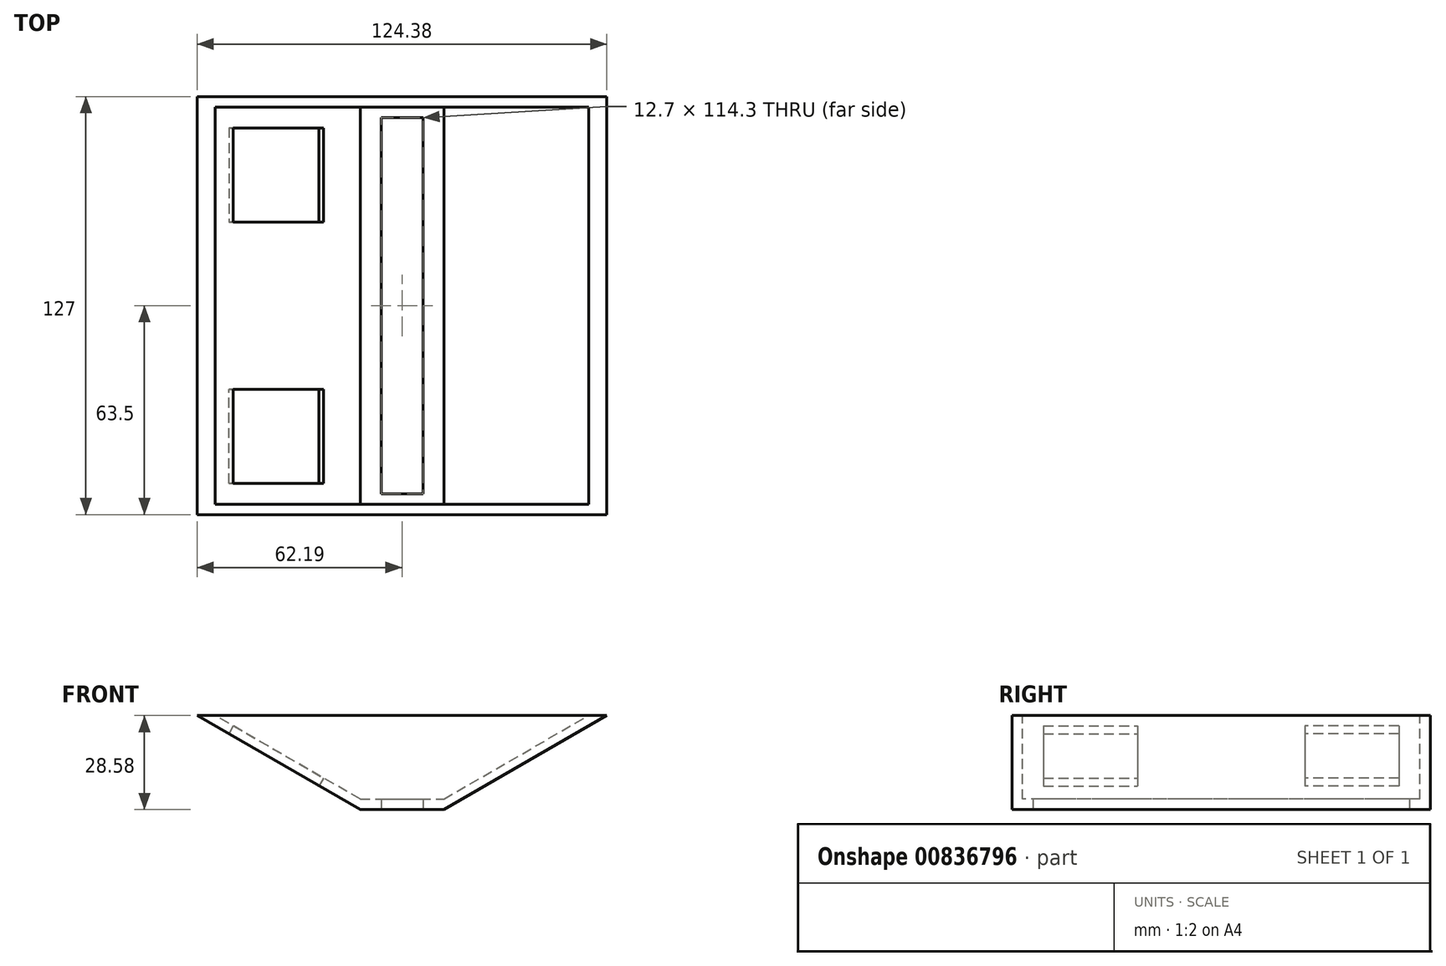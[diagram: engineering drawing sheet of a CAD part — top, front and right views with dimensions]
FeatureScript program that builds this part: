
annotation { "Feature Type Name" : "Feature", "Feature Type Description" : "" }
export const myFeature = defineFeature(function(context is Context, id is Id, definition is map)
    precondition{}
    {
        {
            var Q0;
            Q0=qCreatedBy(makeId("Top.planeOp"),FACE);
            var sketch = newSketch(context, id + "F0", { "sketchPlane" : qUnion([Q0])});
            skLineSegment(sketch, "E0.bottom", {"start": v(-12.7, 63.5) * mm, "end": v(12.7, 63.5) * mm});
            skLineSegment(sketch, "E0.top", {"start": v(-12.7, -63.5) * mm, "end": v(12.7, -63.5) * mm});
            skLineSegment(sketch, "E0.left", {"start": v(-12.7, 63.5) * mm, "end": v(-12.7, -63.5) * mm});
            skLineSegment(sketch, "E0.right", {"start": v(12.7, 63.5) * mm, "end": v(12.7, -63.5) * mm});
            skLineSegment(sketch, "E1.bottom", {"start": v(-6.35, 57.15) * mm, "end": v(6.35, 57.15) * mm});
            skLineSegment(sketch, "E1.top", {"start": v(-6.35, -57.15) * mm, "end": v(6.35, -57.15) * mm});
            skLineSegment(sketch, "E1.left", {"start": v(-6.35, 57.15) * mm, "end": v(-6.35, -57.15) * mm});
            skLineSegment(sketch, "E1.right", {"start": v(6.35, 57.15) * mm, "end": v(6.35, -57.15) * mm});
            skSolve(sketch);
        }
        {
            var Q0;
            Q0 = qSketchRegion(id + "F0", true);
            extrude(context, id + "F1", {"entities" : qUnion([Q0]), "depth" : 3.17 * mm, "offsetDistance" : 25.4 * mm});
        }
        {
            var Q0;
            Q0=qCreatedBy(makeId("Front.planeOp"),FACE);
            var sketch = newSketch(context, id + "F2", { "sketchPlane" : qUnion([Q0])});
            skLineSegment(sketch, "E2", {"start": v(12.7, 3.18) * mm, "end": v(56.7, 28.58) * mm});
            skLineSegment(sketch, "E3", {"start": v(12.7, 3.17) * mm, "end": v(56.7, 3.17) * mm});
            skLineSegment(sketch, "E4", {"start": v(12.7, 0) * mm, "end": v(62.2, 28.58) * mm});
            skLineSegment(sketch, "E5", {"start": v(56.7, 28.58) * mm, "end": v(62.2, 28.58) * mm});
            skLineSegment(sketch, "E6.MirrorCS", {"start": v(-56.7, 28.58) * mm, "end": v(-62.2, 28.58) * mm});
            skLineSegment(sketch, "E7.MirrorCS", {"start": v(-12.7, 0) * mm, "end": v(-62.2, 28.58) * mm});
            skLineSegment(sketch, "E8.MirrorCS", {"start": v(-12.7, 3.17) * mm, "end": v(-56.7, 28.58) * mm});
            skLineSegment(sketch, "E9", {"start": v(-12.7, 0) * mm, "end": v(-12.7, 3.18) * mm});
            skLineSegment(sketch, "E10", {"start": v(12.7, 3.18) * mm, "end": v(12.7, 0) * mm});
            skSolve(sketch);
        }
        {
            var Q0;
            Q0 = qSketchRegion(id + "F2", true);
            extrude(context, id + "F3", {"entities" : qUnion([Q0]), "operationType" : NewBodyOperationType.ADD, "depth" : 63.5 * mm, "offsetDistance" : 25.4 * mm, "hasSecondDirection" : true, "secondDirectionOppositeDirection" : true, "secondDirectionDepth" : 63.5 * mm});
        }
        {
            var Q0;
            Q0=qCreatedBy(makeId("Front.planeOp"),FACE);
            cPlane(context, id + "F4", {"entities" : qUnion([Q0]), "cplaneType" : CPlaneType.OFFSET, "offset" : 63.5 * mm, "width" : 152.4 * mm, "height" : 152.4 * mm});
        }
        {
            var Q0;
            Q0=qCreatedBy(makeId("Front.planeOp"),FACE);
            cPlane(context, id + "F5", {"entities" : qUnion([Q0]), "cplaneType" : CPlaneType.OFFSET, "offset" : 63.5 * mm, "oppositeDirection" : true, "width" : 152.4 * mm, "height" : 152.4 * mm});
        }
        {
            var Q0;
            Q0=qCreatedBy(id+"F4.planeOp",FACE);
            var sketch = newSketch(context, id + "F6", { "sketchPlane" : qUnion([Q0])});
            skLineSegment(sketch, "E11", {"start": v(-62.2, 28.58) * mm, "end": v(62.2, 28.58) * mm});
            skLineSegment(sketch, "E12", {"start": v(-62.2, 28.58) * mm, "end": v(-12.7, 0) * mm});
            skLineSegment(sketch, "E13", {"start": v(-12.7, 0) * mm, "end": v(12.7, 0) * mm});
            skLineSegment(sketch, "E14", {"start": v(12.7, 0) * mm, "end": v(62.2, 28.58) * mm});
            skSolve(sketch);
        }
        {
            var Q0;
            Q0 = qSketchRegion(id + "F6", true);
            extrude(context, id + "F7", {"entities" : qUnion([Q0]), "operationType" : NewBodyOperationType.ADD, "oppositeDirection" : true, "depth" : 3.17 * mm, "offsetDistance" : 25.4 * mm});
        }
        {
            var Q0;
            Q0=qCreatedBy(id+"F5.planeOp",FACE);
            var sketch = newSketch(context, id + "F8", { "sketchPlane" : qUnion([Q0])});
            skLineSegment(sketch, "E15", {"start": v(-62.2, 28.58) * mm, "end": v(62.2, 28.58) * mm});
            skLineSegment(sketch, "E16", {"start": v(-62.2, 28.58) * mm, "end": v(-12.7, 0) * mm});
            skLineSegment(sketch, "E17", {"start": v(-12.7, 0) * mm, "end": v(12.7, 0) * mm});
            skLineSegment(sketch, "E18", {"start": v(12.7, 0) * mm, "end": v(62.2, 28.58) * mm});
            skSolve(sketch);
        }
        {
            var Q0;
            Q0 = qSketchRegion(id + "F8", true);
            extrude(context, id + "F9", {"entities" : qUnion([Q0]), "operationType" : NewBodyOperationType.ADD, "depth" : 3.17 * mm, "offsetDistance" : 25.4 * mm});
        }
        {
            var Q0;
            Q0=makeQuery(id+"F3.opExtrude","SWEPT_FACE",FACE,{"disambiguationData":[OSD([sQuery(id+"F2.wireOp",EDGE,"E7.MirrorCS")])]});
            var sketch = newSketch(context, id + "F10", { "sketchPlane" : qUnion([Q0])});
            skLineSegment(sketch, "E19.bottom", {"start": v(-57.04, -53.97) * mm, "end": v(-25.4, -53.97) * mm});
            skLineSegment(sketch, "E19.top", {"start": v(-57.04, -25.4) * mm, "end": v(-25.4, -25.4) * mm});
            skLineSegment(sketch, "E19.left", {"start": v(-57.04, -53.98) * mm, "end": v(-57.04, -25.4) * mm});
            skLineSegment(sketch, "E19.right", {"start": v(-25.4, -53.98) * mm, "end": v(-25.4, -25.4) * mm});
            skLineSegment(sketch, "E20.MirrorCS", {"start": v(-57.04, 53.98) * mm, "end": v(-57.04, 25.4) * mm});
            skLineSegment(sketch, "E21.MirrorCS", {"start": v(-57.04, 25.4) * mm, "end": v(-25.4, 25.4) * mm});
            skLineSegment(sketch, "E22.MirrorCS", {"start": v(-25.4, 53.98) * mm, "end": v(-25.4, 25.4) * mm});
            skLineSegment(sketch, "E23.MirrorCS", {"start": v(-57.04, 53.97) * mm, "end": v(-25.4, 53.97) * mm});
            skSolve(sketch);
        }
        {
            var Q0;
            Q0=makeQuery(id+"F10.imprint","IMPRINT",FACE,{"disambiguationData":[TD([[makeQuery(id+"F10.imprint","IMPRINT",EDGE,{"derivedFrom":sQuery(id+"F10.wireOp",EDGE,"E20.MirrorCS")}),1.0]])]});
            var Q1;
            Q1=makeQuery(id+"F10.imprint","IMPRINT",FACE,{"disambiguationData":[TD([[makeQuery(id+"F10.imprint","IMPRINT",EDGE,{"derivedFrom":sQuery(id+"F10.wireOp",EDGE,"E19.bottom")}),1.0]])]});
            extrude(context, id + "F11", {"entities" : qUnion([Q0, Q1]), "operationType" : NewBodyOperationType.REMOVE, "endBound" : BoundingType.THROUGH_ALL, "oppositeDirection" : true, "depth" : 25.4 * mm, "offsetDistance" : 25.4 * mm});
        }
    });
